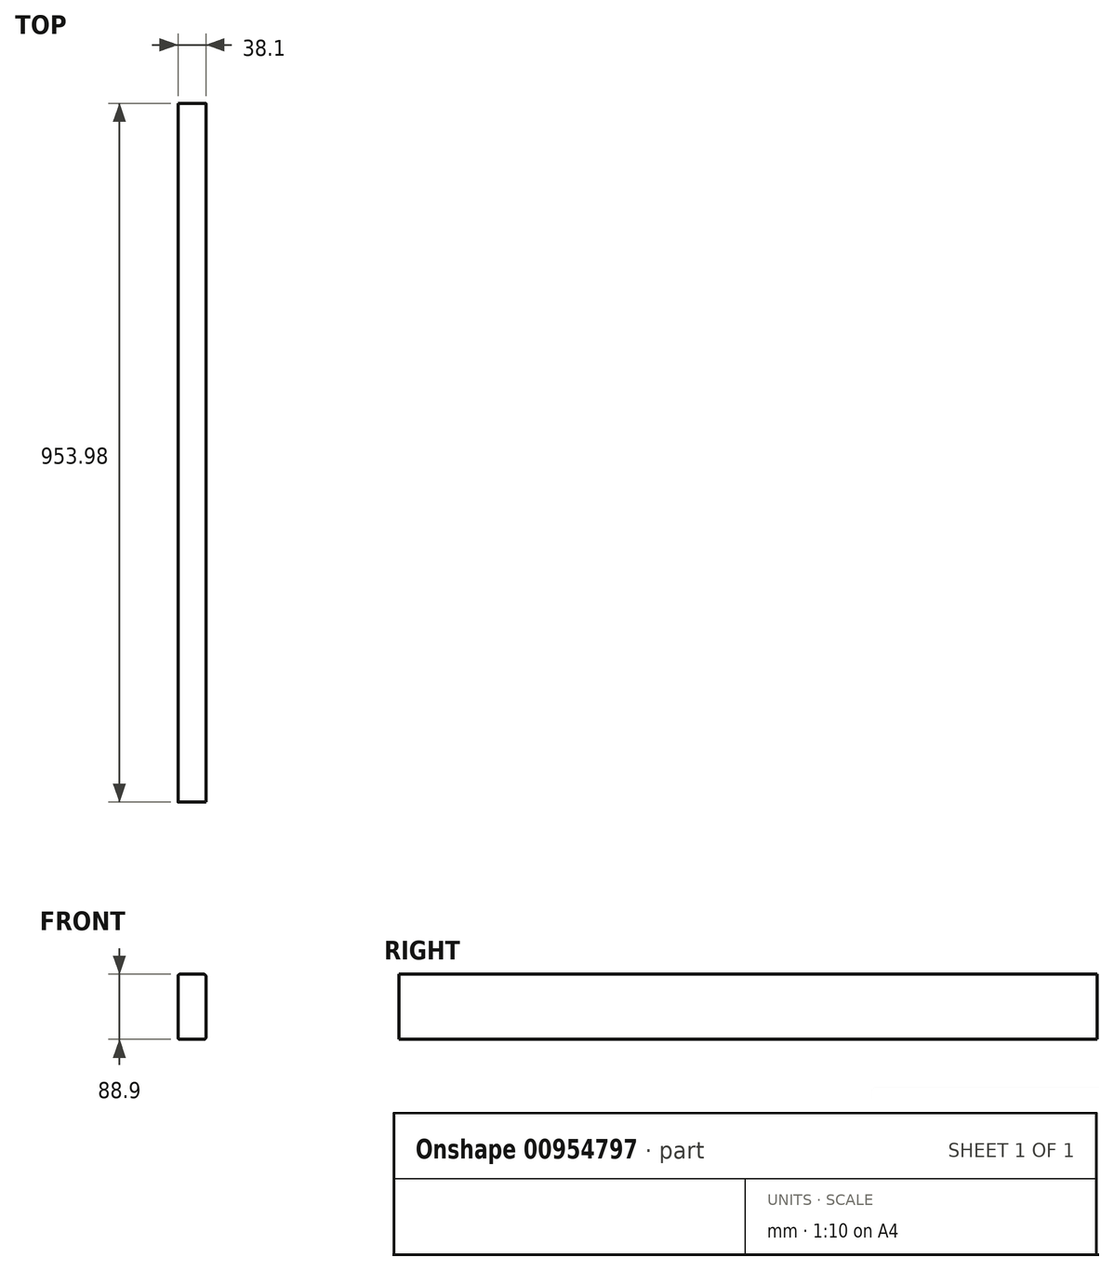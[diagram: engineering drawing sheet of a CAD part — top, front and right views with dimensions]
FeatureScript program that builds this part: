
annotation { "Feature Type Name" : "Feature", "Feature Type Description" : "" }
export const myFeature = defineFeature(function(context is Context, id is Id, definition is map)
    precondition{}
    {
        {
            var Q0;
            Q0=qCreatedBy(makeId("Front.planeOp"),FACE);
            var sketch = newSketch(context, id + "F0", { "sketchPlane" : qUnion([Q0])});
            skLineSegment(sketch, "E0.bottom", {"start": v(19.05, 44.45) * mm, "end": v(-19.05, 44.45) * mm});
            skLineSegment(sketch, "E0.top", {"start": v(19.05, -44.45) * mm, "end": v(-19.05, -44.45) * mm});
            skLineSegment(sketch, "E0.left", {"start": v(19.05, 44.45) * mm, "end": v(19.05, -44.45) * mm});
            skLineSegment(sketch, "E0.right", {"start": v(-19.05, 44.45) * mm, "end": v(-19.05, -44.45) * mm});
            skPoint(sketch, "E0.middle", {"position": v(0, 0) * mm});
            skSolve(sketch);
        }
        {
            var Q0;
            Q0=qSketchRegion(id+"F0",true);
            extrude(context, id + "F1", {"entities" : qUnion([Q0]), "depth" : 75 / 50.8 * mm, "offsetDistance" : 25.4 * mm, "hasSecondDirection" : true, "secondDirectionOppositeDirection" : true, "secondDirectionDepth" : 952.5 * mm});
        }
        {
            var Q0;
            Q0=makeQuery(id+"F1.opExtrude","SWEPT_FACE",FACE,{"disambiguationData":[OSD([sQuery(id+"F0.wireOp",EDGE,"E0.left")])]});
            var sketch = newSketch(context, id + "F2", { "sketchPlane" : qUnion([Q0])});
            skCircle(sketch, "E1", {"center": v(-933.45, 22.22) * mm, "radius": 3.18 * mm});
            skLineSegment(sketch, "E2.bottom", {"start": v(-952.5, 44.45) * mm, "end": v(-914.4, 44.45) * mm, "construction": true});
            skLineSegment(sketch, "E2.top", {"start": v(-952.5, -44.45) * mm, "end": v(-914.4, -44.45) * mm, "construction": true});
            skLineSegment(sketch, "E2.left", {"start": v(-952.5, 44.45) * mm, "end": v(-952.5, -44.45) * mm, "construction": true});
            skLineSegment(sketch, "E2.right", {"start": v(-914.4, 44.45) * mm, "end": v(-914.4, -44.45) * mm, "construction": true});
            skLineSegment(sketch, "E3", {"start": v(-952.5, 22.22) * mm, "end": v(-914.4, 22.22) * mm, "construction": true});
            skSolve(sketch);
        }
        {
            var Q0;
            Q0=qSketchRegion(id+"F2",true);
            extrude(context, id + "F3", {"entities" : qUnion([Q0]), "operationType" : NewBodyOperationType.REMOVE, "oppositeDirection" : true, "depth" : 12.7 * mm, "offsetDistance" : 25.4 * mm});
        }
        {
            var Q0;
            Q0=makeQuery(id+"F1.opExtrude","SWEPT_EDGE",EDGE,{"disambiguationData":[OSD([sQuery(id+"F0.wireOp",EDGE,"E0.bottom"),sQuery(id+"F0.wireOp",EDGE,"E0.left")])]});
            var Q1;
            Q1=makeQuery(id+"F1.opExtrude","SWEPT_EDGE",EDGE,{"disambiguationData":[OSD([sQuery(id+"F0.wireOp",EDGE,"E0.bottom"),sQuery(id+"F0.wireOp",EDGE,"E0.right")])]});
            var Q2;
            Q2=makeQuery(id+"F1.opExtrude","SWEPT_EDGE",EDGE,{"disambiguationData":[OSD([sQuery(id+"F0.wireOp",EDGE,"E0.top"),sQuery(id+"F0.wireOp",EDGE,"E0.left")])]});
            var Q3;
            Q3=makeQuery(id+"F1.opExtrude","SWEPT_EDGE",EDGE,{"disambiguationData":[OSD([sQuery(id+"F0.wireOp",EDGE,"E0.top"),sQuery(id+"F0.wireOp",EDGE,"E0.right")])]});
            fillet(context, id + "F4", {"entities" : qUnion([Q0, Q1, Q2, Q3]), "radius" : 2.54 * mm, "tangentPropagation" : true, "allowEdgeOverflow" : false});
        }
    });
